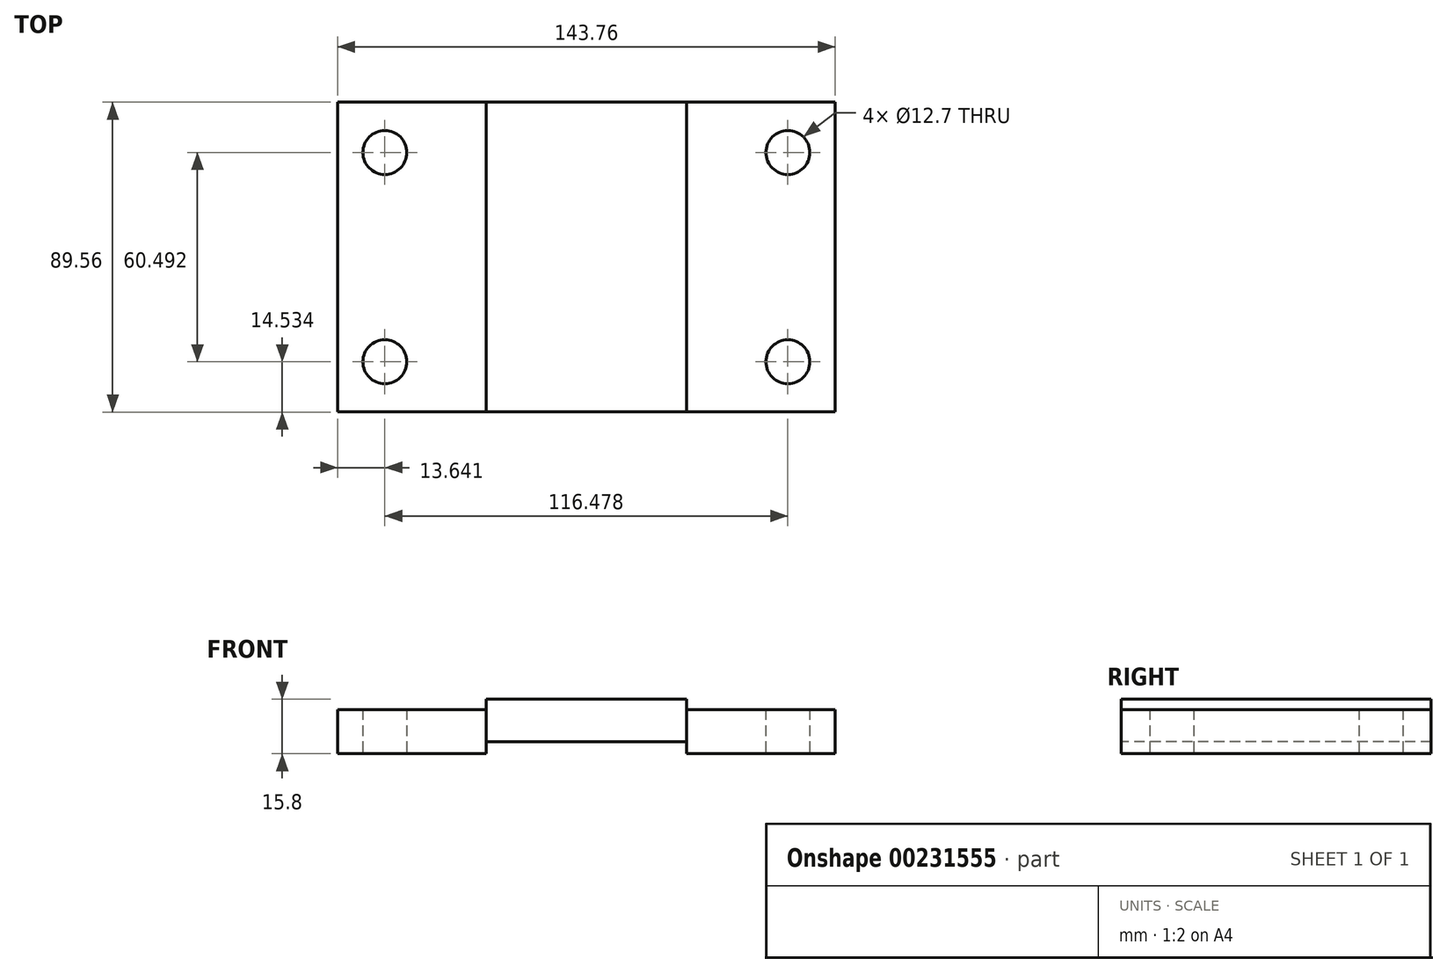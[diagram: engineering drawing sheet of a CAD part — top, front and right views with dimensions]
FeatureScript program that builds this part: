
annotation { "Feature Type Name" : "Feature", "Feature Type Description" : "" }
export const myFeature = defineFeature(function(context is Context, id is Id, definition is map)
    precondition{}
    {
        {
            var Q0;
            Q0=qCreatedBy(makeId("Top.planeOp"),FACE);
            var sketch = newSketch(context, id + "F0", { "sketchPlane" : qUnion([Q0])});
            skLineSegment(sketch, "E0.bottom", {"start": v(71.88, -44.78) * mm, "end": v(-71.88, -44.78) * mm});
            skLineSegment(sketch, "E0.top", {"start": v(71.88, 44.78) * mm, "end": v(-71.88, 44.78) * mm});
            skLineSegment(sketch, "E0.left", {"start": v(71.88, -44.78) * mm, "end": v(71.88, 44.78) * mm});
            skLineSegment(sketch, "E0.right", {"start": v(-71.88, -44.78) * mm, "end": v(-71.88, 44.78) * mm});
            skPoint(sketch, "E0.middle", {"position": v(0, 0) * mm});
            skLineSegment(sketch, "E1", {"start": v(-29, 44.78) * mm, "end": v(-29, -44.78) * mm});
            skLineSegment(sketch, "E2", {"start": v(29, 44.78) * mm, "end": v(29, -44.78) * mm});
            skCircle(sketch, "E3", {"center": v(-58.24, 30.25) * mm, "radius": 6.35 * mm});
            skCircle(sketch, "E4", {"center": v(-58.24, -30.25) * mm, "radius": 6.35 * mm});
            skCircle(sketch, "E5", {"center": v(58.24, -30.25) * mm, "radius": 6.35 * mm});
            skCircle(sketch, "E6", {"center": v(58.24, 30.25) * mm, "radius": 6.35 * mm});
            skSolve(sketch);
        }
        {
            var Q0;
            {var subQ1=sQuery(id+"F0.wireOp",EDGE,"E0.right");Q0=makeQuery(id+"F0.imprint","IMPRINT",FACE,{"disambiguationData":[TD([[makeQuery(id+"F0.imprint","IMPRINT",EDGE,{"derivedFrom":subQ1}),-1.0]])]});}
            var Q1;
            {var subQ1=sQuery(id+"F0.wireOp",EDGE,"E0.left");Q1=makeQuery(id+"F0.imprint","IMPRINT",FACE,{"disambiguationData":[TD([[makeQuery(id+"F0.imprint","IMPRINT",EDGE,{"derivedFrom":subQ1}),1.0]])]});}
            extrude(context, id + "F1", {"entities" : qUnion([Q0, Q1]), "depth" : 12.8 * mm});
        }
        {
            var Q0;
            {var subQ0=sQuery(id+"F0.wireOp",EDGE,"E1");Q0=makeQuery(id+"F0.imprint","IMPRINT",FACE,{"disambiguationData":[TD([[makeQuery(id+"F0.imprint","IMPRINT",EDGE,{"derivedFrom":subQ0}),1.0]])]});}
            extrude(context, id + "F2", {"entities" : qUnion([Q0]), "depth" : 15.8 * mm});
        }
        {
            var Q0;
            {var subQ0=sQuery(id+"F0.wireOp",EDGE,"E1");Q0=makeQuery(id+"F0.imprint","IMPRINT",FACE,{"disambiguationData":[TD([[makeQuery(id+"F0.imprint","IMPRINT",EDGE,{"derivedFrom":subQ0}),1.0]])]});}
            extrude(context, id + "F3", {"entities" : qUnion([Q0]), "operationType" : NewBodyOperationType.REMOVE, "depth" : 3.5 * mm});
        }
    });
